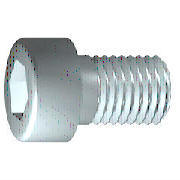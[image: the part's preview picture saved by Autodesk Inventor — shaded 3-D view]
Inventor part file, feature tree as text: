
AUTODESK INVENTOR PART (.ipt)
format: ipt  version: 2022 (Build 260153000, 153)  size: 197,120 bytes
history: native  units: mm (DEFAULTED — no unit token found)
features: sketch x2, extrude x1, plane x1, fillet x1
ambient origin geometry x7: Origin, YZ Plane, XY Plane, X Axis, Y Axis, Z Axis, Center Point
bodies: Solid1 (feature_tree), Body (feature_tree)
feature tree (5):
  extrude  "Slot"  Depth=3.0mm
  plane  "Work Plane1"
  fillet  "Fillet2"  Radius=3.0mm
  sketch  "Sketch1"  dims[d1=8.75mm d2=0.306825mm d3=3.0mm]
  sketch  "Sketch2"  dims[d4=1.3mm d5=60.0deg d6=3.0mm d7=3.0mm d8=2.886751mm d9=5.5mm d10=90.0deg d11=10.0mm d12=0.0mm d13=8.75mm d14=0.0mm d15=0.306725mm d16=0.306725mm d17=0.3mm d19=0.0mm d26=10.0mm d27=45.0deg d28=0.0mm d29=0.0mm d30=0.1mm]
